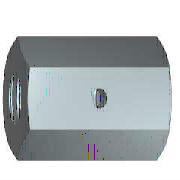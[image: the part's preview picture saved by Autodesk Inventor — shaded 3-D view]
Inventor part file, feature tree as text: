
AUTODESK INVENTOR PART (.ipt)
format: ipt  version: 2023 (Build 270158000, 158)  size: 186,368 bytes
history: native  units: mm (DEFAULTED — no unit token found)
features: sketch x4, hole x1, chamfer x1, extrude x1, other x1, plane x1
ambient origin geometry x7: Origin, YZ Plane, XY Plane, X Axis, Y Axis, Z Axis, Center Point
bodies: Solid1 (feature_tree), Body (feature_tree)
feature tree (9):
  sketch  "Sketch2"  dims[d7=90.0deg]
  hole  "Thread"  [1 undecoded]
  chamfer  "Chamfer1"  Angle=30.0deg  [1 undecoded]
  extrude  "Hole"  Depth=9.525mm
  other  "Work Axis1"
  plane  "Work Plane1"
  sketch  "Sketch1"  dims[d1=19.05mm d2=0.0mm]
  sketch  "Sketch3"  dims[d22=4.9784mm d23=6.0mm d24=4.0mm d25=2.0mm d26=14.3117mm d27=8.0mm d28=20.594885mm]
  sketch  "Sketch4"  dims[d8=0.687408mm d9=30.0deg d10=0.687408mm d11=30.0deg d12=0.0mm d13=0.0mm d14=0.0mm d36=1.905mm d37=9.525mm d38=10.0mm d39=0.0mm d40=9.525mm d45=9.525mm d46=10.998523mm d47=4.363323mm d48=4.363323mm d49=0.687408mm d50=0.687408mm d51=0.0mm]
note: 2 required parameter values undecoded (feature->parameter linkage not recoverable at this tier; creation-order binding heuristic only, values carry confidence <= 0.55)
